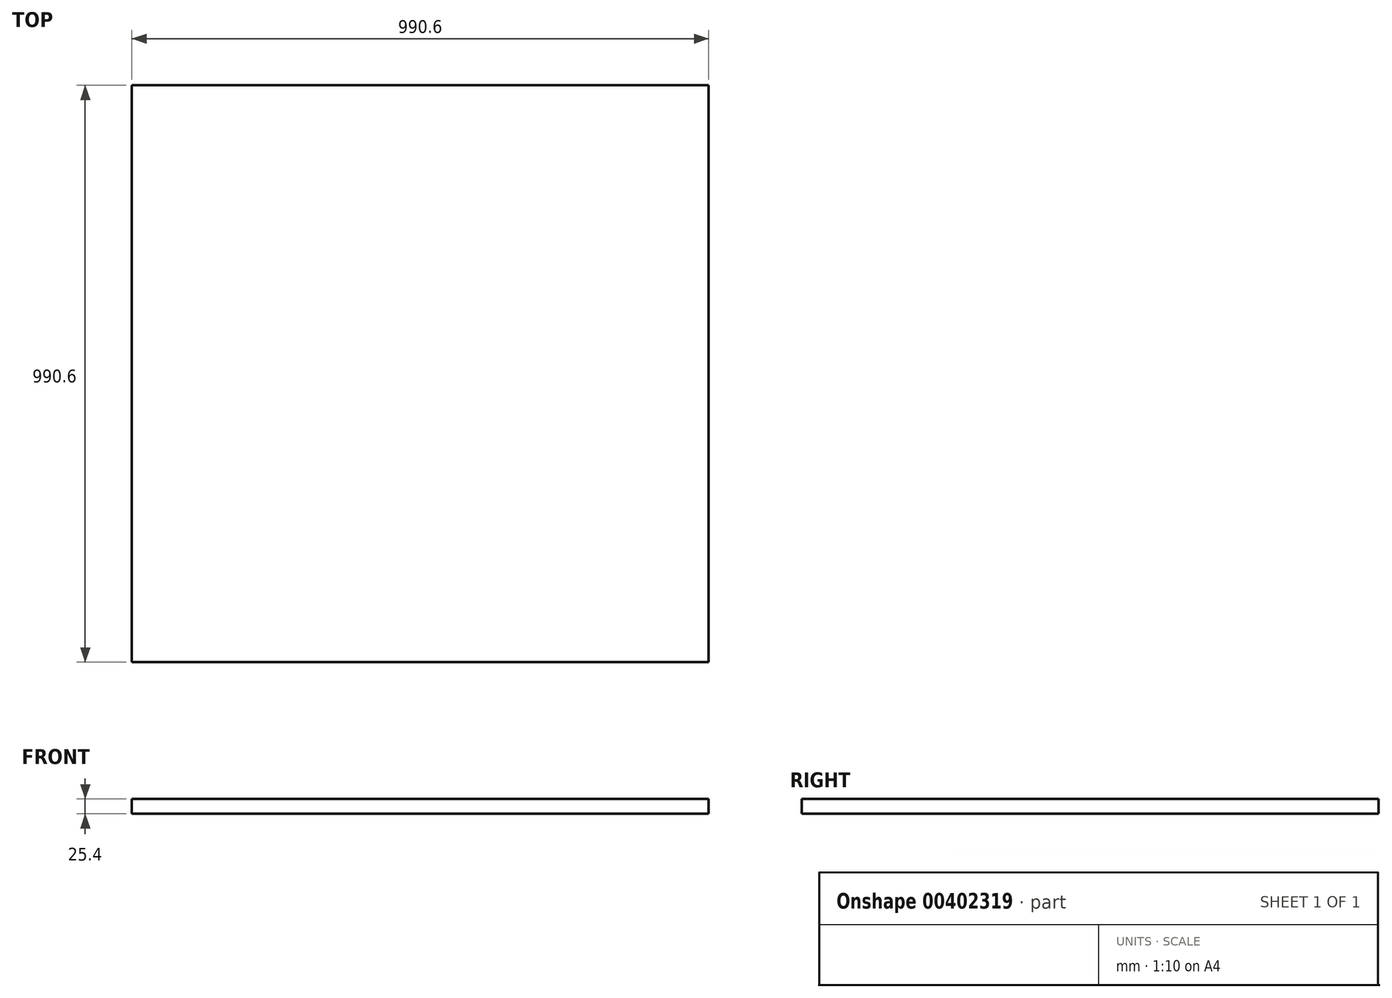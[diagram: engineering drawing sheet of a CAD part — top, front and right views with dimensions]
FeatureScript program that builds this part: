
annotation { "Feature Type Name" : "Feature", "Feature Type Description" : "" }
export const myFeature = defineFeature(function(context is Context, id is Id, definition is map)
    precondition{}
    {
        {
            var Q0;
            Q0=qCreatedBy(makeId("Top.planeOp"),FACE);
            var sketch = newSketch(context, id + "F0", { "sketchPlane" : qUnion([Q0])});
            skLineSegment(sketch, "E0.bottom", {"start": v(-495.3, 495.3) * mm, "end": v(495.3, 495.3) * mm});
            skLineSegment(sketch, "E0.top", {"start": v(-495.3, -495.3) * mm, "end": v(495.3, -495.3) * mm});
            skLineSegment(sketch, "E0.left", {"start": v(-495.3, 495.3) * mm, "end": v(-495.3, -495.3) * mm});
            skLineSegment(sketch, "E0.right", {"start": v(495.3, 495.3) * mm, "end": v(495.3, -495.3) * mm});
            skPoint(sketch, "E0.middle", {"position": v(0, 0) * mm});
            skSolve(sketch);
        }
        {
            var Q0;
            Q0 = qSketchRegion(id + "F0", true);
            extrude(context, id + "F1", {"entities" : qUnion([Q0]), "depth" : 25.4 * mm});
        }
    });
